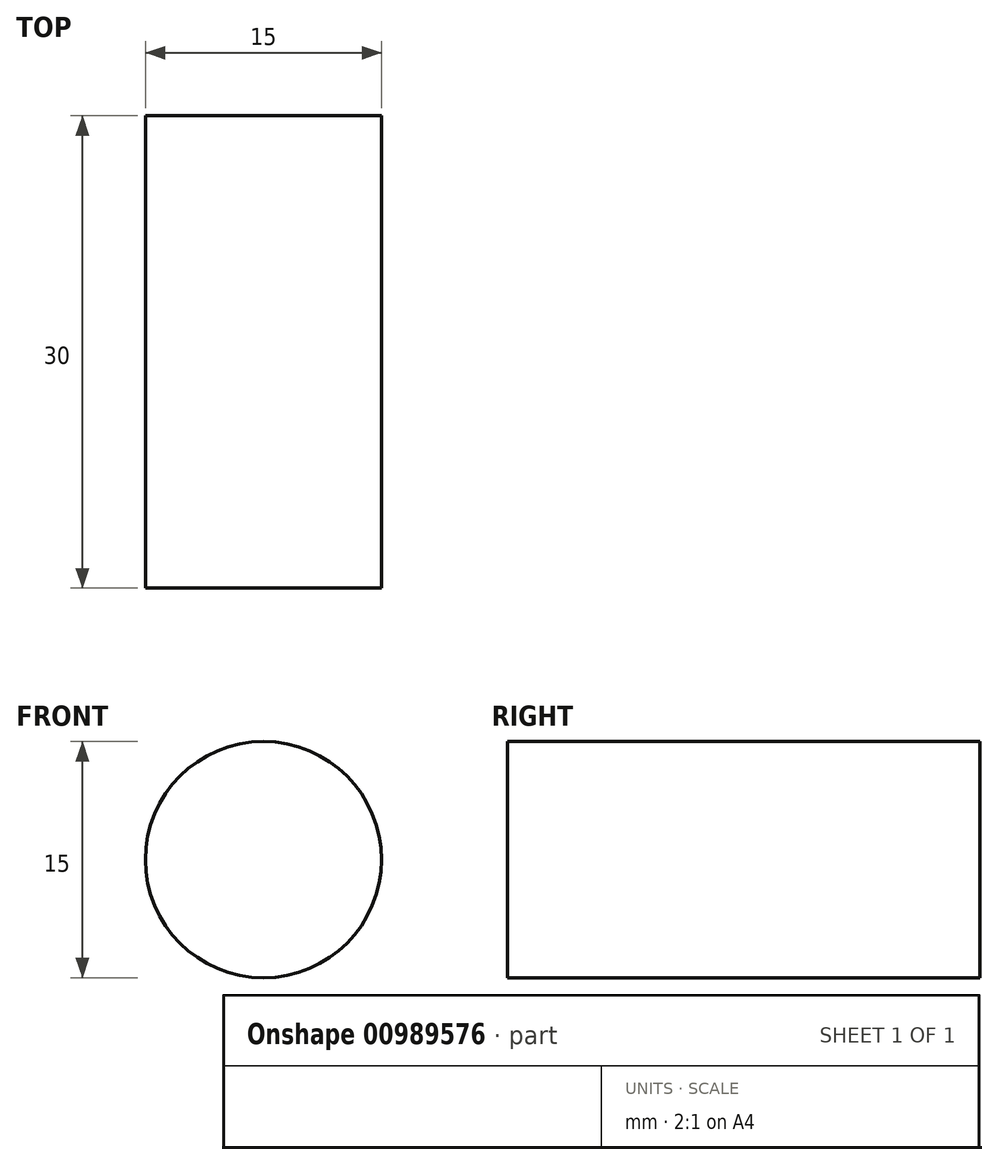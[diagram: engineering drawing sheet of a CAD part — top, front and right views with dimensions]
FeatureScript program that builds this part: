
annotation { "Feature Type Name" : "Feature", "Feature Type Description" : "" }
export const myFeature = defineFeature(function(context is Context, id is Id, definition is map)
    precondition{}
    {
        {
            var Q0;
            Q0=qCreatedBy(makeId("Front.planeOp"),FACE);
            var sketch = newSketch(context, id + "F0", { "sketchPlane" : qUnion([Q0])});
            skCircle(sketch, "E0", {"center": v(0, 0) * mm, "radius": 7.5 * mm});
            skSolve(sketch);
        }
        {
            var Q0;
            Q0 = qSketchRegion(id + "F0", true);
            extrude(context, id + "F1", {"entities" : qUnion([Q0]), "oppositeDirection" : true, "depth" : 30 * mm, "offsetDistance" : 25 * mm});
        }
    });
